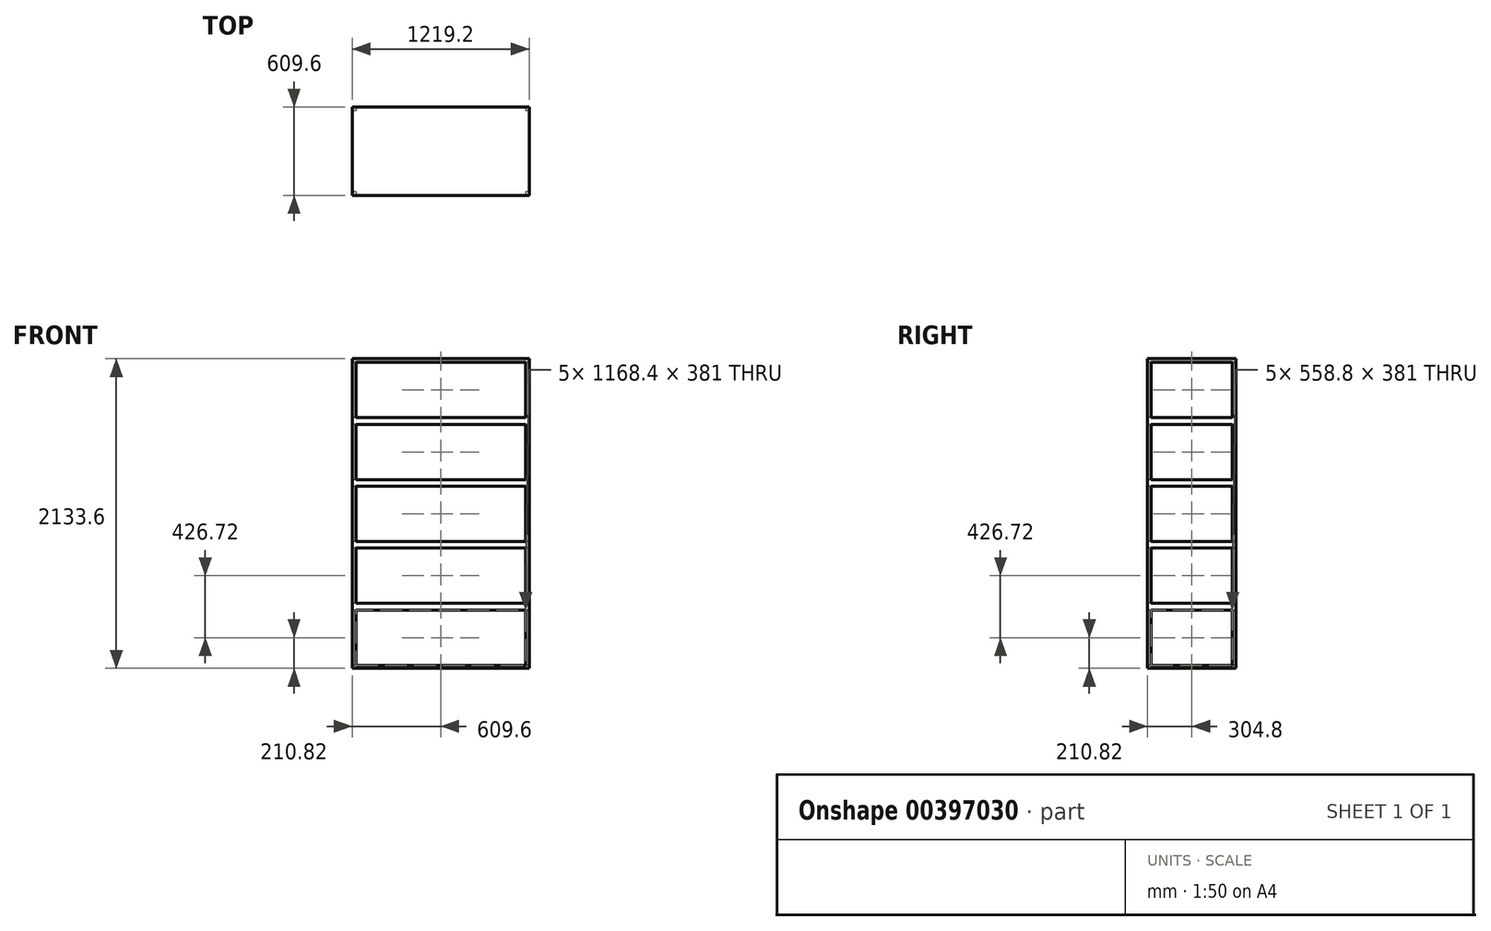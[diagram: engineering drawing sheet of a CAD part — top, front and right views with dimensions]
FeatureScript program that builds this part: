
annotation { "Feature Type Name" : "Feature", "Feature Type Description" : "" }
export const myFeature = defineFeature(function(context is Context, id is Id, definition is map)
    precondition{}
    {
        {
            var Q0;
            Q0=qCreatedBy(makeId("Front.planeOp"),FACE);
            var sketch = newSketch(context, id + "F0", { "sketchPlane" : qUnion([Q0])});
            skLineSegment(sketch, "E0.bottom", {"start": v(-609.6, -1066.8) * mm, "end": v(609.6, -1066.8) * mm});
            skLineSegment(sketch, "E0.top", {"start": v(-609.6, 1066.8) * mm, "end": v(609.6, 1066.8) * mm});
            skLineSegment(sketch, "E0.left", {"start": v(-609.6, -1066.8) * mm, "end": v(-609.6, 1066.8) * mm});
            skLineSegment(sketch, "E0.right", {"start": v(609.6, -1066.8) * mm, "end": v(609.6, 1066.8) * mm});
            skLineSegment(sketch, "E1", {"start": v(0, 1066.8) * mm, "end": v(0, -1066.8) * mm, "construction": true});
            skSolve(sketch);
        }
        {
            var Q0;
            Q0 = qSketchRegion(id + "F0", true);
            extrude(context, id + "F1", {"entities" : qUnion([Q0]), "depth" : 609.6 * mm});
        }
        {
            var Q0;
            Q0=makeQuery(id+"F1.opExtrude","CAP_FACE",FACE,{"disambiguationData":[OSD([sQuery(id+"F0.wireOp",EDGE,"E0.bottom"),sQuery(id+"F0.wireOp",EDGE,"E0.top"),sQuery(id+"F0.wireOp",EDGE,"E0.left"),sQuery(id+"F0.wireOp",EDGE,"E0.right")])],"isStart":false});
            var sketch = newSketch(context, id + "F2", { "sketchPlane" : qUnion([Q0])});
            skLineSegment(sketch, "E2.bottom", {"start": v(-584.2, 1041.4) * mm, "end": v(584.2, 1041.4) * mm});
            skLineSegment(sketch, "E2.top", {"start": v(-584.2, 660.4) * mm, "end": v(584.2, 660.4) * mm});
            skLineSegment(sketch, "E2.left", {"start": v(-584.2, 1041.4) * mm, "end": v(-584.2, 660.4) * mm});
            skLineSegment(sketch, "E2.right", {"start": v(584.2, 1041.4) * mm, "end": v(584.2, 660.4) * mm});
            skLineSegment(sketch, "E3.0.1.0", {"start": v(-584.2, 233.68) * mm, "end": v(584.2, 233.68) * mm});
            skLineSegment(sketch, "E3.0.1.1", {"start": v(-584.2, 614.68) * mm, "end": v(-584.2, 233.68) * mm});
            skLineSegment(sketch, "E3.0.1.2", {"start": v(-584.2, 614.68) * mm, "end": v(584.2, 614.68) * mm});
            skLineSegment(sketch, "E3.0.1.3", {"start": v(584.2, 614.68) * mm, "end": v(584.2, 233.68) * mm});
            skLineSegment(sketch, "E3.0.2.0", {"start": v(-584.2, -193.04) * mm, "end": v(584.2, -193.04) * mm});
            skLineSegment(sketch, "E3.0.2.1", {"start": v(-584.2, 187.96) * mm, "end": v(-584.2, -193.04) * mm});
            skLineSegment(sketch, "E3.0.2.2", {"start": v(-584.2, 187.96) * mm, "end": v(584.2, 187.96) * mm});
            skLineSegment(sketch, "E3.0.2.3", {"start": v(584.2, 187.96) * mm, "end": v(584.2, -193.04) * mm});
            skLineSegment(sketch, "E3.0.3.0", {"start": v(-584.2, -619.76) * mm, "end": v(584.2, -619.76) * mm});
            skLineSegment(sketch, "E3.0.3.1", {"start": v(-584.2, -238.76) * mm, "end": v(-584.2, -619.76) * mm});
            skLineSegment(sketch, "E3.0.3.2", {"start": v(-584.2, -238.76) * mm, "end": v(584.2, -238.76) * mm});
            skLineSegment(sketch, "E3.0.3.3", {"start": v(584.2, -238.76) * mm, "end": v(584.2, -619.76) * mm});
            skLineSegment(sketch, "E3.0.4.0", {"start": v(-584.2, -1046.48) * mm, "end": v(584.2, -1046.48) * mm});
            skLineSegment(sketch, "E3.0.4.1", {"start": v(-584.2, -665.48) * mm, "end": v(-584.2, -1046.48) * mm});
            skLineSegment(sketch, "E3.0.4.2", {"start": v(-584.2, -665.48) * mm, "end": v(584.2, -665.48) * mm});
            skLineSegment(sketch, "E3.0.4.3", {"start": v(584.2, -665.48) * mm, "end": v(584.2, -1046.48) * mm});
            skLineSegment(sketch, "E3.direction1", {"start": v(-584.2, 640.08) * mm, "end": v(-558.8, 640.08) * mm, "construction": true});
            skLineSegment(sketch, "E3.direction2", {"start": v(-584.2, 640.08) * mm, "end": v(-584.2, 213.36) * mm, "construction": true});
            skSolve(sketch);
        }
        {
            var Q0;
            Q0 = qSketchRegion(id + "F2", true);
            extrude(context, id + "F3", {"entities" : qUnion([Q0]), "operationType" : NewBodyOperationType.REMOVE, "endBound" : BoundingType.THROUGH_ALL, "oppositeDirection" : true, "depth" : 25.4 * mm});
        }
        {
            var Q0;
            Q0=makeQuery(id+"F1.opExtrude","SWEPT_FACE",FACE,{"disambiguationData":[OSD([sQuery(id+"F0.wireOp",EDGE,"E0.left")])]});
            var sketch = newSketch(context, id + "F4", { "sketchPlane" : qUnion([Q0])});
            skLineSegment(sketch, "E4.bottom", {"start": v(25.4, 1041.4) * mm, "end": v(584.2, 1041.4) * mm});
            skLineSegment(sketch, "E4.top", {"start": v(25.4, 660.4) * mm, "end": v(584.2, 660.4) * mm});
            skLineSegment(sketch, "E4.left", {"start": v(25.4, 1041.4) * mm, "end": v(25.4, 660.4) * mm});
            skLineSegment(sketch, "E4.right", {"start": v(584.2, 1041.4) * mm, "end": v(584.2, 660.4) * mm});
            skLineSegment(sketch, "E5.0.1.0", {"start": v(25.4, 233.68) * mm, "end": v(584.2, 233.68) * mm});
            skLineSegment(sketch, "E5.0.1.1", {"start": v(25.4, 614.68) * mm, "end": v(25.4, 233.68) * mm});
            skLineSegment(sketch, "E5.0.1.2", {"start": v(25.4, 614.68) * mm, "end": v(584.2, 614.68) * mm});
            skLineSegment(sketch, "E5.0.1.3", {"start": v(584.2, 614.68) * mm, "end": v(584.2, 233.68) * mm});
            skLineSegment(sketch, "E5.0.2.0", {"start": v(25.4, -193.04) * mm, "end": v(584.2, -193.04) * mm});
            skLineSegment(sketch, "E5.0.2.1", {"start": v(25.4, 187.96) * mm, "end": v(25.4, -193.04) * mm});
            skLineSegment(sketch, "E5.0.2.2", {"start": v(25.4, 187.96) * mm, "end": v(584.2, 187.96) * mm});
            skLineSegment(sketch, "E5.0.2.3", {"start": v(584.2, 187.96) * mm, "end": v(584.2, -193.04) * mm});
            skLineSegment(sketch, "E5.0.3.0", {"start": v(25.4, -619.76) * mm, "end": v(584.2, -619.76) * mm});
            skLineSegment(sketch, "E5.0.3.1", {"start": v(25.4, -238.76) * mm, "end": v(25.4, -619.76) * mm});
            skLineSegment(sketch, "E5.0.3.2", {"start": v(25.4, -238.76) * mm, "end": v(584.2, -238.76) * mm});
            skLineSegment(sketch, "E5.0.3.3", {"start": v(584.2, -238.76) * mm, "end": v(584.2, -619.76) * mm});
            skLineSegment(sketch, "E5.0.4.0", {"start": v(25.4, -1046.48) * mm, "end": v(584.2, -1046.48) * mm});
            skLineSegment(sketch, "E5.0.4.1", {"start": v(25.4, -665.48) * mm, "end": v(25.4, -1046.48) * mm});
            skLineSegment(sketch, "E5.0.4.2", {"start": v(25.4, -665.48) * mm, "end": v(584.2, -665.48) * mm});
            skLineSegment(sketch, "E5.0.4.3", {"start": v(584.2, -665.48) * mm, "end": v(584.2, -1046.48) * mm});
            skLineSegment(sketch, "E5.direction1", {"start": v(25.4, 660.4) * mm, "end": v(50.8, 660.4) * mm, "construction": true});
            skLineSegment(sketch, "E5.direction2", {"start": v(25.4, 660.4) * mm, "end": v(25.4, 233.68) * mm, "construction": true});
            skSolve(sketch);
        }
        {
            var Q0;
            Q0 = qSketchRegion(id + "F4", true);
            extrude(context, id + "F5", {"entities" : qUnion([Q0]), "operationType" : NewBodyOperationType.REMOVE, "endBound" : BoundingType.THROUGH_ALL, "oppositeDirection" : true, "depth" : 25.4 * mm});
        }
    });
